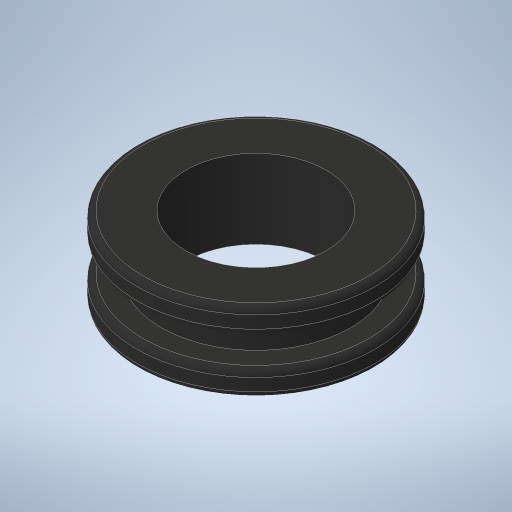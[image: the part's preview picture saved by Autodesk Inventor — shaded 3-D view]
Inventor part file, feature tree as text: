
AUTODESK INVENTOR PART (.ipt)
format: ipt  version: 2023.4 (Build 274418000, 418)  size: 271,360 bytes
history: native  units: in
note: dims shown in document units (in); Inventor stores cm internally (conversion verified against a paired STEP export)
features: revolve x1, fillet x1, sketch x1
ambient origin geometry x8: Origin, YZ Plane, XZ Plane, XY Plane, X Axis, Y Axis, Z Axis, Center Point
bodies: Solid1 (feature_tree)
feature tree (3):
  revolve  "Revolution1"  [1 undecoded]
  fillet  "Fillet1"  Radius=0.2in
  sketch  "Sketch1"  dims[d0=0.24in d1=0.075in d2=0.2in d3=0.0625in d4=0.0625in d5=0.0625in d6=90.0deg d7=0.0156in]
note: 1 required parameter value undecoded (feature->parameter linkage not recoverable at this tier; creation-order binding heuristic only, values carry confidence <= 0.55)
